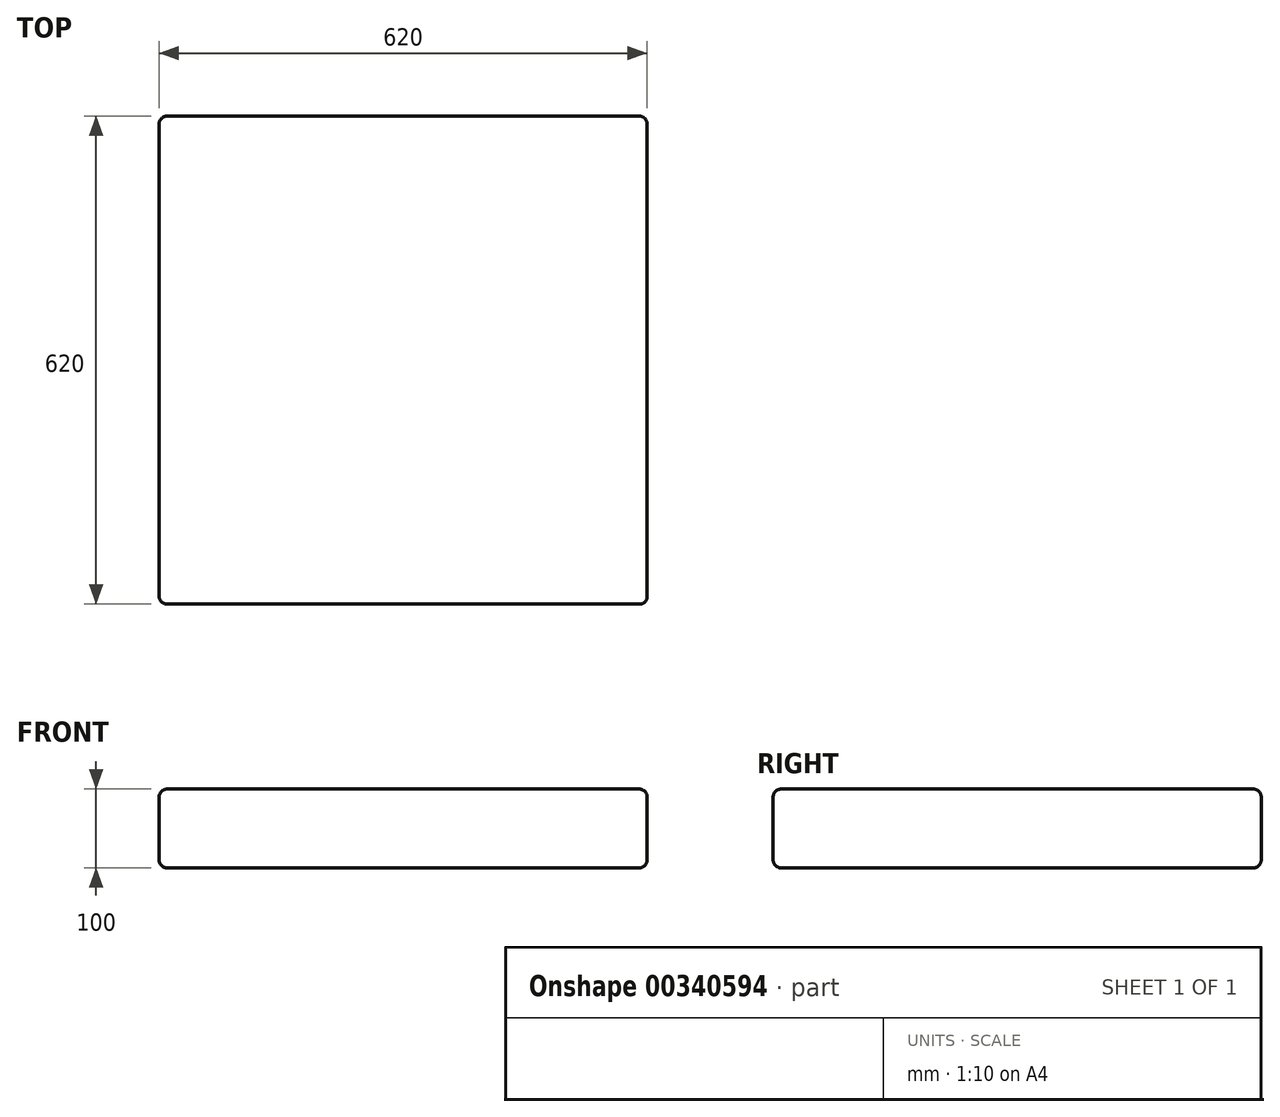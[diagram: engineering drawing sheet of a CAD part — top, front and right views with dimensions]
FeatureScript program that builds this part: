
annotation { "Feature Type Name" : "Feature", "Feature Type Description" : "" }
export const myFeature = defineFeature(function(context is Context, id is Id, definition is map)
    precondition{}
    {
        {
            var Q0;
            Q0=qCreatedBy(makeId("Top.planeOp"),FACE);
            var sketch = newSketch(context, id + "F0", { "sketchPlane" : qUnion([Q0])});
            skLineSegment(sketch, "E0.bottom", {"start": v(-34.51, 584.2) * mm, "end": v(585.49, 584.2) * mm});
            skLineSegment(sketch, "E0.top", {"start": v(-34.51, -35.8) * mm, "end": v(585.49, -35.8) * mm});
            skLineSegment(sketch, "E0.left", {"start": v(-34.51, 584.2) * mm, "end": v(-34.51, -35.8) * mm});
            skLineSegment(sketch, "E0.right", {"start": v(585.49, 584.2) * mm, "end": v(585.49, -35.8) * mm});
            skSolve(sketch);
        }
        {
            var Q0;
            Q0 = qSketchRegion(id + "F0", true);
            extrude(context, id + "F1", {"entities" : qUnion([Q0]), "depth" : 100 * mm});
        }
        {
            var Q0;
            Q0=makeQuery(id+"F1.opExtrude","SWEPT_EDGE",EDGE,{"disambiguationData":[OSD([sQuery(id+"F0.wireOp",EDGE,"E0.top"),sQuery(id+"F0.wireOp",EDGE,"E0.right")])]});
            var Q1;
            Q1=makeQuery(id+"F1.opExtrude","CAP_FACE",FACE,{"disambiguationData":[OSD([sQuery(id+"F0.wireOp",EDGE,"E0.bottom"),sQuery(id+"F0.wireOp",EDGE,"E0.top"),sQuery(id+"F0.wireOp",EDGE,"E0.left"),sQuery(id+"F0.wireOp",EDGE,"E0.right")])],"isStart":false});
            var Q2;
            Q2=makeQuery(id+"F1.opExtrude","SWEPT_EDGE",EDGE,{"disambiguationData":[OSD([sQuery(id+"F0.wireOp",EDGE,"E0.top"),sQuery(id+"F0.wireOp",EDGE,"E0.left")])]});
            var Q3;
            Q3=makeQuery(id+"F1.opExtrude","CAP_FACE",FACE,{"disambiguationData":[OSD([sQuery(id+"F0.wireOp",EDGE,"E0.bottom"),sQuery(id+"F0.wireOp",EDGE,"E0.top"),sQuery(id+"F0.wireOp",EDGE,"E0.left"),sQuery(id+"F0.wireOp",EDGE,"E0.right")])],"isStart":true});
            var Q4;
            Q4=makeQuery(id+"F1.opExtrude","SWEPT_FACE",FACE,{"disambiguationData":[OSD([sQuery(id+"F0.wireOp",EDGE,"E0.bottom")])]});
            var Q5;
            Q5=makeQuery(id+"F1.opExtrude","SWEPT_EDGE",EDGE,{"disambiguationData":[OSD([sQuery(id+"F0.wireOp",EDGE,"E0.bottom"),sQuery(id+"F0.wireOp",EDGE,"E0.left")])]});
            var Q6;
            Q6=makeQuery(id+"F1.opExtrude","SWEPT_FACE",FACE,{"disambiguationData":[OSD([sQuery(id+"F0.wireOp",EDGE,"E0.top")])]});
            var Q7;
            Q7=makeQuery(id+"F1.opExtrude","SWEPT_FACE",FACE,{"disambiguationData":[OSD([sQuery(id+"F0.wireOp",EDGE,"E0.left")])]});
            var Q8;
            Q8=makeQuery(id+"F1.opExtrude","SWEPT_FACE",FACE,{"disambiguationData":[OSD([sQuery(id+"F0.wireOp",EDGE,"E0.right")])]});
            var Q9;
            Q9=makeQuery(id+"F1.opExtrude","CAP_EDGE",EDGE,{"disambiguationData":[OSD([sQuery(id+"F0.wireOp",EDGE,"E0.left")])],"isStart":true});
            var Q10;
            Q10=makeQuery(id+"F1.opExtrude","CAP_EDGE",EDGE,{"disambiguationData":[OSD([sQuery(id+"F0.wireOp",EDGE,"E0.left")])],"isStart":false});
            var Q11;
            Q11=makeQuery(id+"F1.opExtrude","CAP_EDGE",EDGE,{"disambiguationData":[OSD([sQuery(id+"F0.wireOp",EDGE,"E0.right")])],"isStart":false});
            var Q12;
            Q12=makeQuery(id+"F1.opExtrude","SWEPT_EDGE",EDGE,{"disambiguationData":[OSD([sQuery(id+"F0.wireOp",EDGE,"E0.bottom"),sQuery(id+"F0.wireOp",EDGE,"E0.right")])]});
            var Q13;
            Q13=makeQuery(id+"F1.opExtrude","CAP_EDGE",EDGE,{"disambiguationData":[OSD([sQuery(id+"F0.wireOp",EDGE,"E0.bottom")])],"isStart":true});
            var Q14;
            Q14=makeQuery(id+"F1.opExtrude","CAP_EDGE",EDGE,{"disambiguationData":[OSD([sQuery(id+"F0.wireOp",EDGE,"E0.bottom")])],"isStart":false});
            var Q15;
            Q15=makeQuery(id+"F1.opExtrude","CAP_EDGE",EDGE,{"disambiguationData":[OSD([sQuery(id+"F0.wireOp",EDGE,"E0.top")])],"isStart":true});
            var Q16;
            Q16=makeQuery(id+"F1.opExtrude","CAP_EDGE",EDGE,{"disambiguationData":[OSD([sQuery(id+"F0.wireOp",EDGE,"E0.top")])],"isStart":false});
            var Q17;
            Q17=makeQuery(id+"F1.opExtrude","CAP_EDGE",EDGE,{"disambiguationData":[OSD([sQuery(id+"F0.wireOp",EDGE,"E0.right")])],"isStart":true});
            fillet(context, id + "F2", {"entities" : qUnion([Q0, Q1, Q2, Q3, Q4, Q5, Q6, Q7, Q8, Q9, Q10, Q11, Q12, Q13, Q14, Q15, Q16, Q17]), "radius" : 10 * mm, "tangentPropagation" : true, "allowEdgeOverflow" : false});
        }
    });
